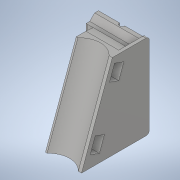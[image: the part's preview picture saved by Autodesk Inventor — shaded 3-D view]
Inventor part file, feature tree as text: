
AUTODESK INVENTOR PART (.ipt)
format: ipt  version: 2021.1 (Build 251245010, 245A)  size: 146,432 bytes
history: mixed  units: in
note: dims shown in document units (in); Inventor stores cm internally (conversion verified against a paired STEP export)
features: move_body x2, direct_edit x1, extrude x1, sketch x1, imported_body x1
ambient origin geometry x8: Origin, YZ Plane, XZ Plane, XY Plane, X Axis, Y Axis, Z Axis, Center Point
bodies: Solid1 (imported_parasolid), Body1 (imported_parasolid)
feature tree (6):
  direct_edit  "Direktbearbeitung2"
  extrude  "Extrusion1"  Depth=0.5906in TaperAngle=0.0deg
  sketch  "Skizze1"  dims[d3=0.0in d4=0.0in d5=0.1181in d6=0.5906in d7=0.0in d8=0.0in d9=0.0in d10=0.2283in]
  move_body  "Verschieben2"
  move_body  "Verschieben3"
  imported_body  NMx_Import_Brep_tag  [imported B-rep: ~43 faces, bbox_mm=[31.0, 51.6, 41.280864]]
